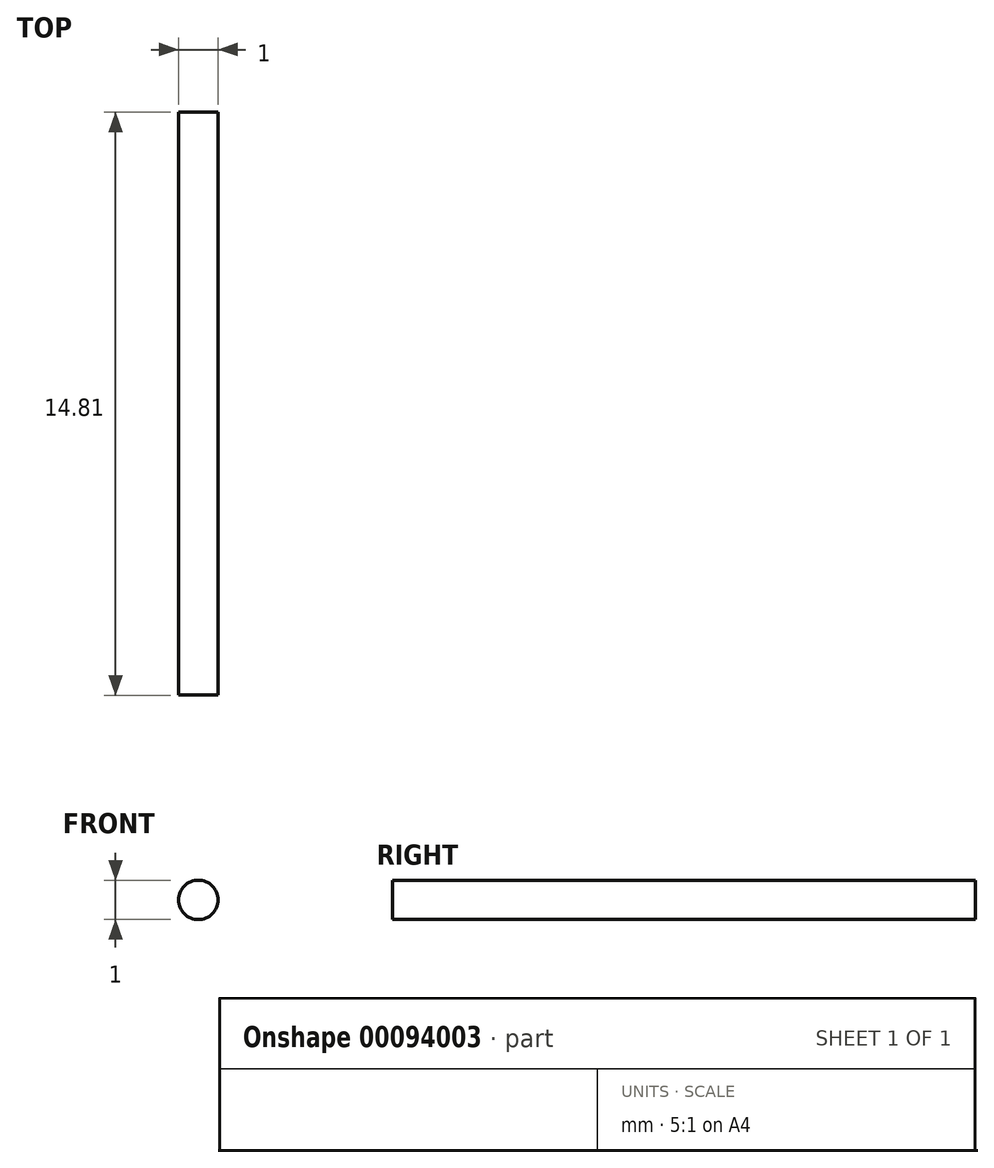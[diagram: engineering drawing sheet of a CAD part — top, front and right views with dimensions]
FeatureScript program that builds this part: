
annotation { "Feature Type Name" : "Feature", "Feature Type Description" : "" }
export const myFeature = defineFeature(function(context is Context, id is Id, definition is map)
    precondition{}
    {
        {
            var Q0;
            Q0=qCreatedBy(makeId("Front.planeOp"),FACE);
            var sketch = newSketch(context, id + "F0", { "sketchPlane" : qUnion([Q0])});
            skCircle(sketch, "E0", {"center": v(0, 0) * mm, "radius": 0.5 * mm});
            skSolve(sketch);
        }
        {
            var Q0;
            Q0=makeQuery(id+"F0.imprint","IMPRINT",FACE,{"disambiguationData":[TD([[makeQuery(id+"F0.imprint","IMPRINT",EDGE,{"derivedFrom":sQuery(id+"F0.wireOp",EDGE,"E0")}),1.0]])]});
            extrude(context, id + "F1", {"entities" : qUnion([Q0]), "depth" : 14.8 * mm});
        }
    });
